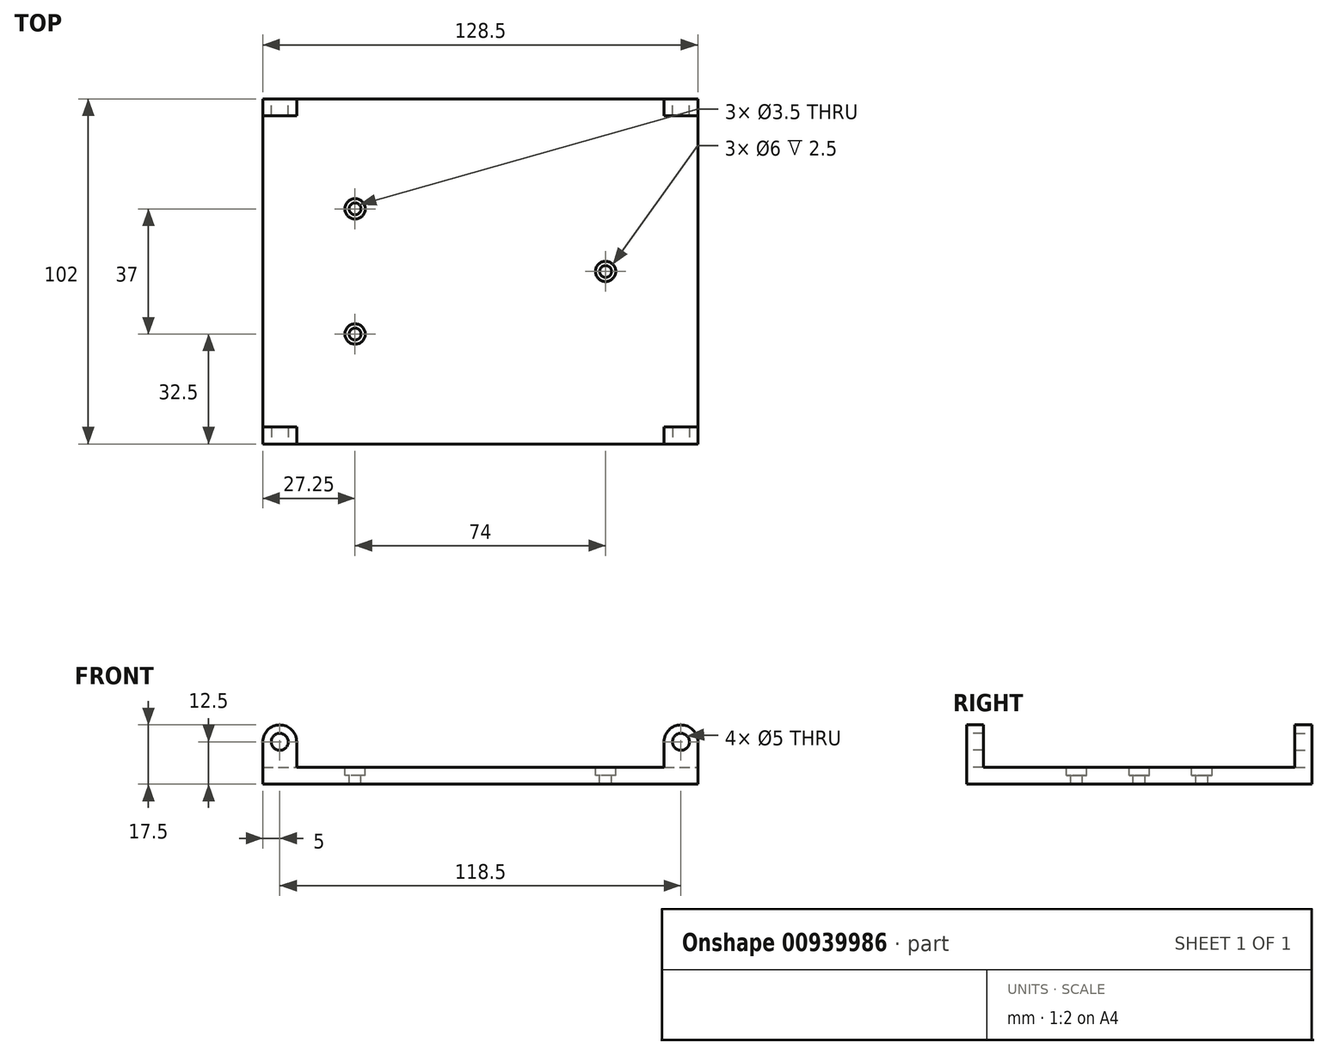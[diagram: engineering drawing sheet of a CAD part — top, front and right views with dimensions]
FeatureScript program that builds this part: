
annotation { "Feature Type Name" : "Feature", "Feature Type Description" : "" }
export const myFeature = defineFeature(function(context is Context, id is Id, definition is map)
    precondition{}
    {
        {
            var Q0;
            Q0=qCreatedBy(makeId("Top.planeOp"),FACE);
            var sketch = newSketch(context, id + "F0", { "sketchPlane" : qUnion([Q0])});
            skLineSegment(sketch, "E0.bottom", {"start": v(-64.25, 51) * mm, "end": v(64.25, 51) * mm});
            skLineSegment(sketch, "E0.top", {"start": v(-64.25, -51) * mm, "end": v(64.25, -51) * mm});
            skLineSegment(sketch, "E0.left", {"start": v(-64.25, 51) * mm, "end": v(-64.25, -51) * mm});
            skLineSegment(sketch, "E0.right", {"start": v(64.25, 51) * mm, "end": v(64.25, -51) * mm});
            skPoint(sketch, "E0.middle", {"position": v(0, 0) * mm});
            skSolve(sketch);
        }
        {
            var Q0;
            Q0=makeQuery(id+"F0.imprint","IMPRINT",FACE,{"disambiguationData":[TD([[makeQuery(id+"F0.imprint","IMPRINT",EDGE,{"derivedFrom":sQuery(id+"F0.wireOp",EDGE,"E0.bottom")}),-1.0]])]});
            extrude(context, id + "F1", {"entities" : qUnion([Q0]), "depth" : 5 * mm, "offsetDistance" : 25 * mm});
        }
        {
            var Q0;
            Q0=makeQuery(id+"F1.opExtrude","SWEPT_FACE",FACE,{"disambiguationData":[OSD([sQuery(id+"F0.wireOp",EDGE,"E0.top")])]});
            var sketch = newSketch(context, id + "F2", { "sketchPlane" : qUnion([Q0])});
            skLineSegment(sketch, "E1", {"start": v(0, 0) * mm, "end": v(0, 19.43) * mm, "construction": true});
            skLineSegment(sketch, "E2", {"start": v(-64.25, 5) * mm, "end": v(-64.25, 12.5) * mm});
            skArc(sketch, "E3", {"start": v(-54.25, 12.5) * mm, "mid": v(-59.25, 17.5) * mm, "end": v(-64.25, 12.5) * mm});
            skLineSegment(sketch, "E4", {"start": v(-54.25, 12.5) * mm, "end": v(-54.25, 5) * mm});
            skLineSegment(sketch, "E5.MirrorCS", {"start": v(64.25, 5) * mm, "end": v(64.25, 12.5) * mm});
            skLineSegment(sketch, "E6.MirrorCS", {"start": v(54.25, 12.5) * mm, "end": v(54.25, 5) * mm});
            skArc(sketch, "E7.MirrorCS", {"start": v(54.25, 12.5) * mm, "mid": v(59.25, 17.5) * mm, "end": v(64.25, 12.5) * mm});
            skSolve(sketch);
        }
        {
            var Q0;
            {var subQ0=sQuery(id+"F2.wireOp",EDGE,"E2");Q0=makeQuery(id+"F2.imprint","IMPRINT",FACE,{"disambiguationData":[TD([[makeQuery(id+"F2.imprint","IMPRINT",EDGE,{"derivedFrom":subQ0}),-1.0]])]});}
            var Q1;
            {var subQ0=sQuery(id+"F2.wireOp",EDGE,"E5.MirrorCS");Q1=makeQuery(id+"F2.imprint","IMPRINT",FACE,{"disambiguationData":[TD([[makeQuery(id+"F2.imprint","IMPRINT",EDGE,{"derivedFrom":subQ0}),1.0]])]});}
            extrude(context, id + "F3", {"entities" : qUnion([Q0, Q1]), "operationType" : NewBodyOperationType.ADD, "oppositeDirection" : true, "depth" : 5 * mm, "offsetDistance" : 25 * mm});
        }
        {
            var Q0;
            {var subQ0=sQuery(id+"F0.wireOp",EDGE,"E0.top");Q0=makeQuery(id+"F3.boolean.opBoolean","MERGE",FACE,{"derivedFrom":[makeQuery(id+"F1.opExtrude","SWEPT_FACE",FACE,{"disambiguationData":[OSD([subQ0])]}),makeQuery(id+"F3.opExtrude","CAP_FACE",FACE,{"disambiguationData":[OSD([subQ0,sQuery(id+"F2.wireOp",EDGE,"E2"),sQuery(id+"F2.wireOp",EDGE,"E3"),sQuery(id+"F2.wireOp",EDGE,"E4")])],"isStart":true}),makeQuery(id+"F3.opExtrude","CAP_FACE",FACE,{"disambiguationData":[OSD([subQ0,sQuery(id+"F2.wireOp",EDGE,"E5.MirrorCS"),sQuery(id+"F2.wireOp",EDGE,"E6.MirrorCS"),sQuery(id+"F2.wireOp",EDGE,"E7.MirrorCS")])],"isStart":true})]});}
            var sketch = newSketch(context, id + "F4", { "sketchPlane" : qUnion([Q0])});
            skPoint(sketch, "E8", {"position": v(-59.25, 12.5) * mm});
            skPoint(sketch, "E9", {"position": v(59.25, 12.5) * mm});
            skSolve(sketch);
        }
        {
            var Q0;
            Q0=sQuery(id+"F4.wireOp",VERTEX,"E8");
            var Q1;
            Q1=sQuery(id+"F4.wireOp",VERTEX,"E9");
            var Q2;
            Q2=makeQuery(id+"F1.opExtrude","SWEPT_BODY",BODY,{"disambiguationData":[OSD([sQuery(id+"F0.wireOp",EDGE,"E0.bottom"),sQuery(id+"F0.wireOp",EDGE,"E0.top"),sQuery(id+"F0.wireOp",EDGE,"E0.left"),sQuery(id+"F0.wireOp",EDGE,"E0.right")])]});
            hole(context, id + "F5", {"style" : HoleStyle.SIMPLE, "endStyle" : HoleEndStyle.THROUGH, "holeDiameter" : 5 * mm, "majorDiameter" : 5 * mm, "isTappedThrough" : true, "tappedDepth" : 12 * mm, "tapClearance" : 3, "locations" : qUnion([Q0, Q1]), "scope" : qUnion([Q2])});
        }
        {
            var Q0;
            Q0=makeQuery(id+"F1.opExtrude","SWEPT_BODY",BODY,{"disambiguationData":[OSD([sQuery(id+"F0.wireOp",EDGE,"E0.bottom"),sQuery(id+"F0.wireOp",EDGE,"E0.top"),sQuery(id+"F0.wireOp",EDGE,"E0.left"),sQuery(id+"F0.wireOp",EDGE,"E0.right")])]});
            var Q1;
            Q1=qCreatedBy(makeId("Front.planeOp"),FACE);
            mirror(context, id + "F6", {"operationType" : NewBodyOperationType.ADD, "entities" : qUnion([Q0]), "mirrorPlane" : qUnion([Q1])});
        }
        {
            var Q0;
            Q0=makeQuery(id+"F1.opExtrude","CAP_FACE",FACE,{"disambiguationData":[OSD([sQuery(id+"F0.wireOp",EDGE,"E0.bottom"),sQuery(id+"F0.wireOp",EDGE,"E0.top"),sQuery(id+"F0.wireOp",EDGE,"E0.left"),sQuery(id+"F0.wireOp",EDGE,"E0.right")])],"isStart":false});
            var sketch = newSketch(context, id + "F7", { "sketchPlane" : qUnion([Q0])});
            skPoint(sketch, "E10", {"position": v(-37, 18.5) * mm});
            skPoint(sketch, "E11", {"position": v(-37, -18.5) * mm});
            skPoint(sketch, "E12", {"position": v(37, 0) * mm});
            skLineSegment(sketch, "E13", {"start": v(-37, 18.5) * mm, "end": v(-37, -18.5) * mm, "construction": true});
            skLineSegment(sketch, "E14", {"start": v(37, 0) * mm, "end": v(-37, 0) * mm, "construction": true});
            skPoint(sketch, "E14.endSnap0", {"position": v(-37, 0) * mm});
            skLineSegment(sketch, "E15", {"start": v(0, 51) * mm, "end": v(0, 0) * mm, "construction": true});
            skSolve(sketch);
        }
        {
            var Q0;
            Q0=sQuery(id+"F7.wireOp",VERTEX,"E10");
            var Q1;
            Q1=sQuery(id+"F7.wireOp",VERTEX,"E11");
            var Q2;
            Q2=sQuery(id+"F7.wireOp",VERTEX,"E12");
            var Q3;
            Q3=makeQuery(id+"F1.opExtrude","SWEPT_BODY",BODY,{"disambiguationData":[OSD([sQuery(id+"F0.wireOp",EDGE,"E0.bottom"),sQuery(id+"F0.wireOp",EDGE,"E0.top"),sQuery(id+"F0.wireOp",EDGE,"E0.left"),sQuery(id+"F0.wireOp",EDGE,"E0.right")])]});
            hole(context, id + "F8", {"style" : HoleStyle.C_BORE, "endStyle" : HoleEndStyle.THROUGH, "holeDiameter" : 3.5 * mm, "cBoreDiameter" : 6 * mm, "cBoreDepth" : 2.5 * mm, "majorDiameter" : 5 * mm, "isTappedThrough" : true, "tappedDepth" : 12 * mm, "tapClearance" : 3, "locations" : qUnion([Q0, Q1, Q2]), "scope" : qUnion([Q3])});
        }
    });
